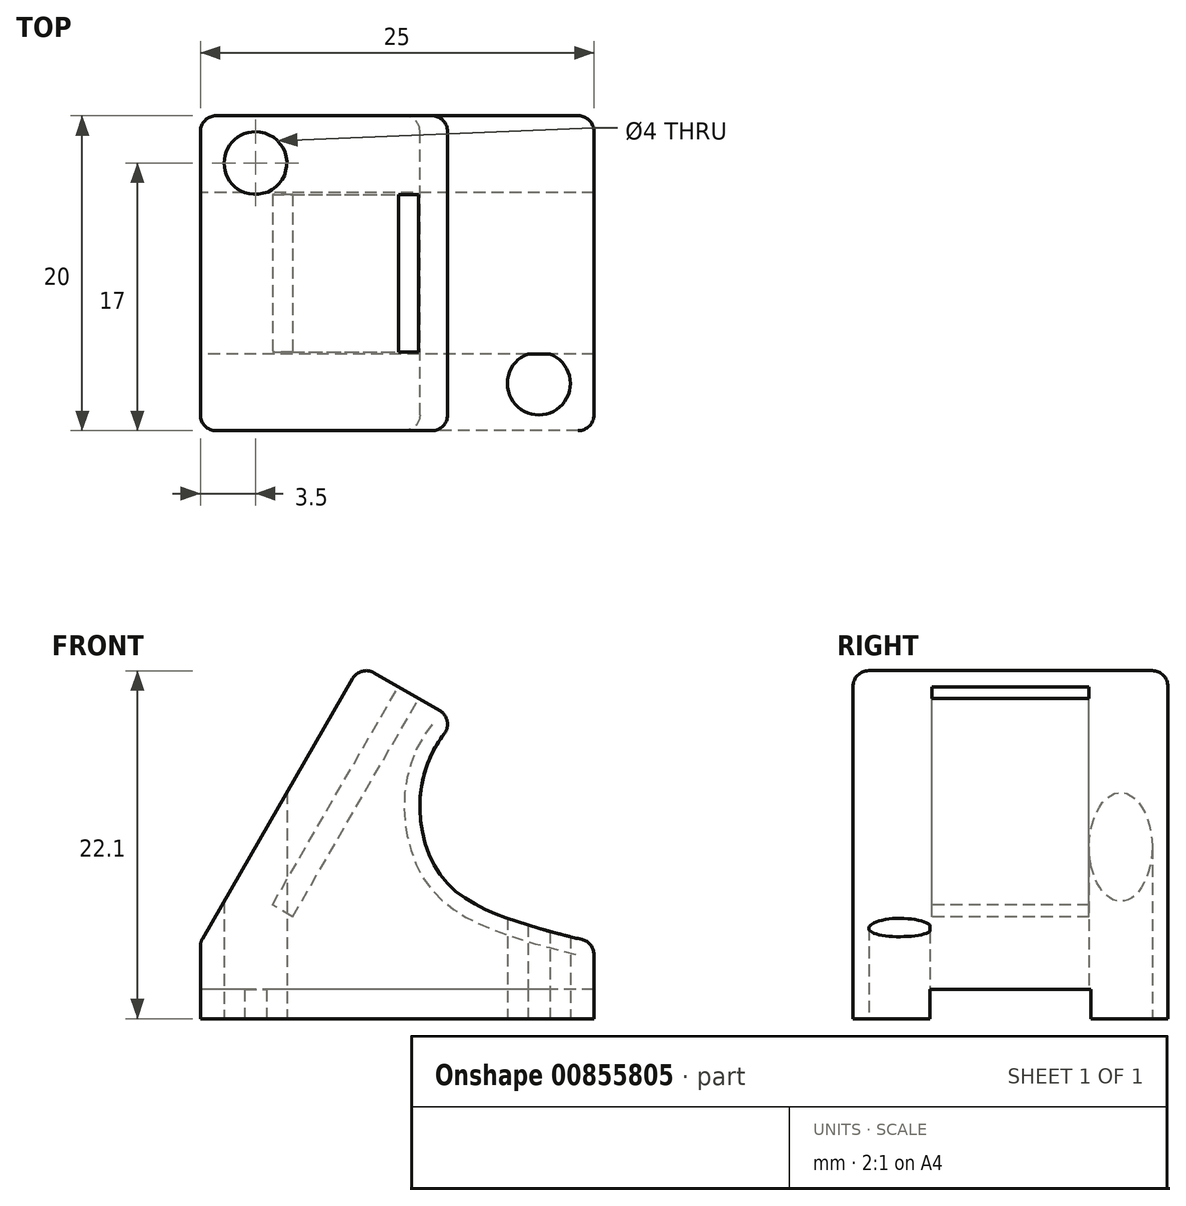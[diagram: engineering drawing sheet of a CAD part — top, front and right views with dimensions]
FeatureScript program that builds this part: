
annotation { "Feature Type Name" : "Feature", "Feature Type Description" : "" }
export const myFeature = defineFeature(function(context is Context, id is Id, definition is map)
    precondition{}
    {
        {
            var Q0;
            Q0=qCreatedBy(makeId("Top.planeOp"),FACE);
            var sketch = newSketch(context, id + "F0", { "sketchPlane" : qUnion([Q0])});
            skLineSegment(sketch, "E0.bottom", {"start": v(12.5, 5.13) * mm, "end": v(-12.5, 5.13) * mm});
            skLineSegment(sketch, "E0.top", {"start": v(12.5, -5.12) * mm, "end": v(-12.5, -5.12) * mm});
            skLineSegment(sketch, "E0.left", {"start": v(12.5, 5.13) * mm, "end": v(12.5, -5.12) * mm});
            skLineSegment(sketch, "E0.right", {"start": v(-12.5, 5.13) * mm, "end": v(-12.5, -5.12) * mm});
            skPoint(sketch, "E0.middle", {"position": v(0, 0) * mm});
            skLineSegment(sketch, "E1.bottom", {"start": v(12.5, 10) * mm, "end": v(-12.5, 10) * mm});
            skLineSegment(sketch, "E1.top", {"start": v(12.5, -10) * mm, "end": v(-12.5, -10) * mm});
            skLineSegment(sketch, "E1.left", {"start": v(12.5, 10) * mm, "end": v(12.5, -10) * mm});
            skLineSegment(sketch, "E1.right", {"start": v(-12.5, 10) * mm, "end": v(-12.5, -10) * mm});
            skSolve(sketch);
        }
        {
            var Q0;
            {var subQ0=sQuery(id+"F0.wireOp",EDGE,"E0.bottom");var subQ1=makeQuery(id+"F0.imprint","IMPRINT",EDGE,{"derivedFrom":subQ0});var subQ2=sQuery(id+"F0.wireOp",EDGE,"E0.top");var subQ3=makeQuery(id+"F0.imprint","IMPRINT",EDGE,{"derivedFrom":subQ2});Q0=qUnion([makeQuery(id+"F0.imprint","IMPRINT",FACE,{"disambiguationData":[TD([[subQ1,-1.0]])]}),makeQuery(id+"F0.imprint","IMPRINT",FACE,{"disambiguationData":[TD([[subQ3,1.0]])]}),makeQuery(id+"F0.imprint","IMPRINT",FACE,{"disambiguationData":[TD([[subQ1,1.0]])]})]);}
            extrude(context, id + "F1", {"entities" : qUnion([Q0]), "depth" : 3 * mm, "offsetDistance" : 25 * mm});
        }
        {
            var Q0;
            {var subQ0=sQuery(id+"F0.wireOp",EDGE,"E0.bottom");Q0=makeQuery(id+"F0.imprint","IMPRINT",FACE,{"disambiguationData":[TD([[makeQuery(id+"F0.imprint","IMPRINT",EDGE,{"derivedFrom":subQ0}),-1.0]])]});}
            var Q1;
            {var subQ0=sQuery(id+"F0.wireOp",EDGE,"E0.top");Q1=makeQuery(id+"F0.imprint","IMPRINT",FACE,{"disambiguationData":[TD([[makeQuery(id+"F0.imprint","IMPRINT",EDGE,{"derivedFrom":subQ0}),1.0]])]});}
            extrude(context, id + "F2", {"entities" : qUnion([Q0, Q1]), "operationType" : NewBodyOperationType.ADD, "oppositeDirection" : true, "depth" : 1.85 * mm, "offsetDistance" : 25 * mm});
        }
        {
            var Q0;
            Q0=qCreatedBy(makeId("Front.planeOp"),FACE);
            var sketch = newSketch(context, id + "F3", { "sketchPlane" : qUnion([Q0])});
            skLineSegment(sketch, "E2.bottom", {"start": v(-12.5, 3) * mm, "end": v(12.5, 3) * mm});
            skLineSegment(sketch, "E2.top", {"start": v(-12.5, -3) * mm, "end": v(12.5, -3) * mm});
            skLineSegment(sketch, "E2.left", {"start": v(-12.5, 3) * mm, "end": v(-12.5, -3) * mm});
            skLineSegment(sketch, "E2.right", {"start": v(12.5, 3) * mm, "end": v(12.5, -3) * mm});
            skPoint(sketch, "E2.middle", {"position": v(0, 0) * mm});
            skFitSpline(sketch, "E3", {"points": [v(12.5, 3) * mm, v(1.97, 8.74) * mm, v(3.77, 17.1) * mm], "startDerivative": vector(-40.02, 9.18) * mm, "endDerivative": vector(17.65, 16.82) * mm});
            skLineSegment(sketch, "E4", {"start": v(3.77, 17.1) * mm, "end": v(-2.33, 20.62) * mm});
            skLineSegment(sketch, "E5", {"start": v(3.77, 17.1) * mm, "end": v(1.08, 14.53) * mm});
            skLineSegment(sketch, "E6", {"start": v(-12.5, 3) * mm, "end": v(-2.33, 20.62) * mm});
            skSolve(sketch);
        }
        {
            var Q0;
            Q0=makeQuery(id+"F3.imprint","IMPRINT",FACE,{"disambiguationData":[TD([[makeQuery(id+"F3.imprint","IMPRINT",EDGE,{"derivedFrom":sQuery(id+"F3.wireOp",EDGE,"E2.bottom")}),1.0]])]});
            extrude(context, id + "F4", {"entities" : qUnion([Q0]), "operationType" : NewBodyOperationType.ADD, "depth" : 10 * mm, "offsetDistance" : 25 * mm, "hasSecondDirection" : true, "secondDirectionOppositeDirection" : true, "secondDirectionDepth" : 10 * mm});
        }
        {
            var Q0;
            Q0=makeQuery(id+"F4.opExtrude","SWEPT_FACE",FACE,{"disambiguationData":[OSD([sQuery(id+"F3.wireOp",EDGE,"E4")])]});
            var sketch = newSketch(context, id + "F5", { "sketchPlane" : qUnion([Q0])});
            skLineSegment(sketch, "E7.bottom", {"start": v(-12.33, -10) * mm, "end": v(-5.28, -10) * mm});
            skLineSegment(sketch, "E7.top", {"start": v(-12.33, 10) * mm, "end": v(-5.28, 10) * mm});
            skLineSegment(sketch, "E7.left", {"start": v(-12.33, -10) * mm, "end": v(-12.33, 10) * mm});
            skLineSegment(sketch, "E7.right", {"start": v(-5.28, -10) * mm, "end": v(-5.28, 10) * mm});
            skLineSegment(sketch, "E8", {"start": v(-5.28, -10) * mm, "end": v(-12.33, 10) * mm});
            skLineSegment(sketch, "E9.bottom", {"start": v(-8.05, 5) * mm, "end": v(-9.55, 5) * mm});
            skLineSegment(sketch, "E9.top", {"start": v(-8.05, -5) * mm, "end": v(-9.55, -5) * mm});
            skLineSegment(sketch, "E9.left", {"start": v(-8.05, 5) * mm, "end": v(-8.05, -5) * mm});
            skLineSegment(sketch, "E9.right", {"start": v(-9.55, 5) * mm, "end": v(-9.55, -5) * mm});
            skPoint(sketch, "E9.middle", {"position": v(-8.8, 0) * mm});
            skSolve(sketch);
        }
        {
            var Q0;
            Q0=makeQuery(id+"F4.opExtrude","CAP_EDGE",EDGE,{"disambiguationData":[OSD([sQuery(id+"F3.wireOp",EDGE,"E6")])],"isStart":false});
            var Q1;
            Q1=makeQuery(id+"F4.opExtrude","SWEPT_EDGE",EDGE,{"disambiguationData":[OSD([sQuery(id+"F3.wireOp",EDGE,"E4"),sQuery(id+"F3.wireOp",EDGE,"E6")])]});
            var Q2;
            Q2=makeQuery(id+"F4.opExtrude","CAP_EDGE",EDGE,{"disambiguationData":[OSD([sQuery(id+"F3.wireOp",EDGE,"E4")])],"isStart":false});
            var Q3;
            Q3=makeQuery(id+"F4.opExtrude","SWEPT_EDGE",EDGE,{"disambiguationData":[OSD([sQuery(id+"F3.wireOp",EDGE,"E3"),sQuery(id+"F3.wireOp",EDGE,"E4")])]});
            var Q4;
            Q4=makeQuery(id+"F4.opExtrude","CAP_EDGE",EDGE,{"disambiguationData":[OSD([sQuery(id+"F3.wireOp",EDGE,"E3")])],"isStart":true});
            var Q5;
            Q5=makeQuery(id+"F4.opExtrude","CAP_EDGE",EDGE,{"disambiguationData":[OSD([sQuery(id+"F3.wireOp",EDGE,"E3")])],"isStart":false});
            var Q6;
            Q6=makeQuery(id+"F4.boolean.opBoolean","MERGE",EDGE,{"derivedFrom":[makeQuery(id+"F1.opExtrude","CAP_EDGE",EDGE,{"disambiguationData":[OSD([sQuery(id+"F0.wireOp",EDGE,"E0.left"),sQuery(id+"F0.wireOp",EDGE,"E1.left")])],"isStart":false}),makeQuery(id+"F4.opExtrude","SWEPT_EDGE",EDGE,{"disambiguationData":[OSD([sQuery(id+"F3.wireOp",EDGE,"E2.bottom"),sQuery(id+"F3.wireOp",EDGE,"E2.right"),sQuery(id+"F3.wireOp",EDGE,"E3")])]})]});
            var Q7;
            {var subQ0=sQuery(id+"F0.wireOp",EDGE,"E1.left");var subQ1=sQuery(id+"F0.wireOp",EDGE,"E1.top");Q7=makeQuery(id+"F2.boolean.opBoolean","MERGE",EDGE,{"derivedFrom":[makeQuery(id+"F1.opExtrude","SWEPT_EDGE",EDGE,{"disambiguationData":[OSD([subQ1,subQ0])]}),makeQuery(id+"F2.opExtrude","SWEPT_EDGE",EDGE,{"disambiguationData":[OSD([subQ1,subQ0])]})]});}
            var Q8;
            {var subQ0=sQuery(id+"F0.wireOp",EDGE,"E1.right");var subQ1=sQuery(id+"F0.wireOp",EDGE,"E1.top");Q8=makeQuery(id+"F2.boolean.opBoolean","MERGE",EDGE,{"derivedFrom":[makeQuery(id+"F1.opExtrude","SWEPT_EDGE",EDGE,{"disambiguationData":[OSD([subQ1,subQ0])]}),makeQuery(id+"F2.opExtrude","SWEPT_EDGE",EDGE,{"disambiguationData":[OSD([subQ1,subQ0])]})]});}
            var Q9;
            {var subQ0=sQuery(id+"F0.wireOp",EDGE,"E1.left");var subQ1=sQuery(id+"F0.wireOp",EDGE,"E1.bottom");Q9=makeQuery(id+"F2.boolean.opBoolean","MERGE",EDGE,{"derivedFrom":[makeQuery(id+"F1.opExtrude","SWEPT_EDGE",EDGE,{"disambiguationData":[OSD([subQ1,subQ0])]}),makeQuery(id+"F2.opExtrude","SWEPT_EDGE",EDGE,{"disambiguationData":[OSD([subQ1,subQ0])]})]});}
            var Q10;
            Q10=makeQuery(id+"F4.boolean.opBoolean","MERGE",EDGE,{"derivedFrom":[makeQuery(id+"F1.opExtrude","CAP_EDGE",EDGE,{"disambiguationData":[OSD([sQuery(id+"F0.wireOp",EDGE,"E0.right"),sQuery(id+"F0.wireOp",EDGE,"E1.right")])],"isStart":false}),makeQuery(id+"F4.opExtrude","SWEPT_EDGE",EDGE,{"disambiguationData":[OSD([sQuery(id+"F3.wireOp",EDGE,"E2.bottom"),sQuery(id+"F3.wireOp",EDGE,"E2.left"),sQuery(id+"F3.wireOp",EDGE,"E6")])]})]});
            var Q11;
            Q11=makeQuery(id+"F4.opExtrude","CAP_EDGE",EDGE,{"disambiguationData":[OSD([sQuery(id+"F3.wireOp",EDGE,"E6")])],"isStart":true});
            var Q12;
            {var subQ0=sQuery(id+"F0.wireOp",EDGE,"E1.right");var subQ1=sQuery(id+"F0.wireOp",EDGE,"E1.bottom");Q12=makeQuery(id+"F2.boolean.opBoolean","MERGE",EDGE,{"derivedFrom":[makeQuery(id+"F1.opExtrude","SWEPT_EDGE",EDGE,{"disambiguationData":[OSD([subQ1,subQ0])]}),makeQuery(id+"F2.opExtrude","SWEPT_EDGE",EDGE,{"disambiguationData":[OSD([subQ1,subQ0])]})]});}
            var Q13;
            Q13=makeQuery(id+"F4.opExtrude","CAP_EDGE",EDGE,{"disambiguationData":[OSD([sQuery(id+"F3.wireOp",EDGE,"E4")])],"isStart":true});
            fillet(context, id + "F6", {"entities" : qUnion([Q0, Q1, Q2, Q3, Q4, Q5, Q6, Q7, Q8, Q9, Q10, Q11, Q12, Q13]), "radius" : 1 * mm, "tangentPropagation" : true, "allowEdgeOverflow" : false});
        }
        {
            var Q0;
            Q0=makeQuery(id+"F2.opExtrude","CAP_FACE",FACE,{"disambiguationData":[OSD([sQuery(id+"F0.wireOp",EDGE,"E0.top"),sQuery(id+"F0.wireOp",EDGE,"E1.top"),sQuery(id+"F0.wireOp",EDGE,"E1.left"),sQuery(id+"F0.wireOp",EDGE,"E1.right")])],"isStart":false});
            var sketch = newSketch(context, id + "F7", { "sketchPlane" : qUnion([Q0])});
            skLineSegment(sketch, "E10", {"start": v(0, 0) * mm, "end": v(-9, 0) * mm});
            skLineSegment(sketch, "E11", {"start": v(-9, 0) * mm, "end": v(-9, -7) * mm});
            skCircle(sketch, "E12", {"center": v(-9, -7) * mm, "radius": 2 * mm});
            skCircle(sketch, "E13.MirrorC", {"center": v(9, -7) * mm, "radius": 2 * mm});
            skCircle(sketch, "E14.MirrorC", {"center": v(9, 7) * mm, "radius": 2 * mm});
            skCircle(sketch, "E15.MirrorC", {"center": v(-9, 7) * mm, "radius": 2 * mm});
            skSolve(sketch);
        }
        {
            var Q0;
            {var subQ0=sQuery(id+"F7.wireOp",EDGE,"E15.MirrorC");var subQ1=makeQuery(id+"F2.opExtrude","CAP_EDGE",EDGE,{"disambiguationData":[OSD([sQuery(id+"F0.wireOp",EDGE,"E0.top")])],"isStart":false});var subQ2=makeQuery(id+"F7.imprint","INTERSECT",VERTEX,{"disambiguationData":[OD(0.0)],"derivedFrom":[subQ1,subQ0]});Q0=makeQuery(id+"F7.imprint","IMPRINT",FACE,{"disambiguationData":[TD([[makeQuery(id+"F7.imprint","IMPRINT",EDGE,{"disambiguationData":[TD([[subQ2,-1.0]])],"derivedFrom":subQ0}),-1.0]])]});}
            var Q1;
            {var subQ0=sQuery(id+"F7.wireOp",EDGE,"E14.MirrorC");var subQ1=makeQuery(id+"F2.opExtrude","CAP_EDGE",EDGE,{"disambiguationData":[OSD([sQuery(id+"F0.wireOp",EDGE,"E0.top")])],"isStart":false});var subQ2=makeQuery(id+"F7.imprint","INTERSECT",VERTEX,{"disambiguationData":[OD(0.0)],"derivedFrom":[subQ1,subQ0]});Q1=makeQuery(id+"F7.imprint","IMPRINT",FACE,{"disambiguationData":[TD([[makeQuery(id+"F7.imprint","IMPRINT",EDGE,{"disambiguationData":[TD([[subQ2,-1.0]])],"derivedFrom":subQ0}),1.0]])]});}
            var Q2;
            Q2=makeQuery(id+"F7.imprint","IMPRINT",FACE,{"disambiguationData":[TD([[makeQuery(id+"F7.imprint","IMPRINT",EDGE,{"derivedFrom":sQuery(id+"F7.wireOp",EDGE,"E13.MirrorC")}),-1.0]])]});
            var Q3;
            Q3=makeQuery(id+"F7.imprint","IMPRINT",FACE,{"disambiguationData":[TD([[makeQuery(id+"F7.imprint","IMPRINT",EDGE,{"derivedFrom":sQuery(id+"F7.wireOp",EDGE,"E12")}),1.0]])]});
            extrude(context, id + "F8", {"entities" : qUnion([Q0, Q1, Q2, Q3]), "operationType" : NewBodyOperationType.REMOVE, "oppositeDirection" : true, "depth" : 17.8 * mm, "offsetDistance" : 25 * mm});
        }
        {
            var Q0;
            {var subQ5=sQuery(id+"F5.wireOp",EDGE,"E9.bottom");Q0=makeQuery(id+"F5.imprint","IMPRINT",FACE,{"disambiguationData":[TD([[makeQuery(id+"F5.imprint","IMPRINT",EDGE,{"derivedFrom":subQ5}),1.0]])]});}
            var Q1;
            {var subQ5=sQuery(id+"F5.wireOp",EDGE,"E9.top");Q1=makeQuery(id+"F5.imprint","IMPRINT",FACE,{"disambiguationData":[TD([[makeQuery(id+"F5.imprint","IMPRINT",EDGE,{"derivedFrom":subQ5}),-1.0]])]});}
            extrude(context, id + "F9", {"entities" : qUnion([Q0, Q1]), "operationType" : NewBodyOperationType.REMOVE, "oppositeDirection" : true, "depth" : 16 * mm, "offsetDistance" : 25 * mm});
        }
    });
